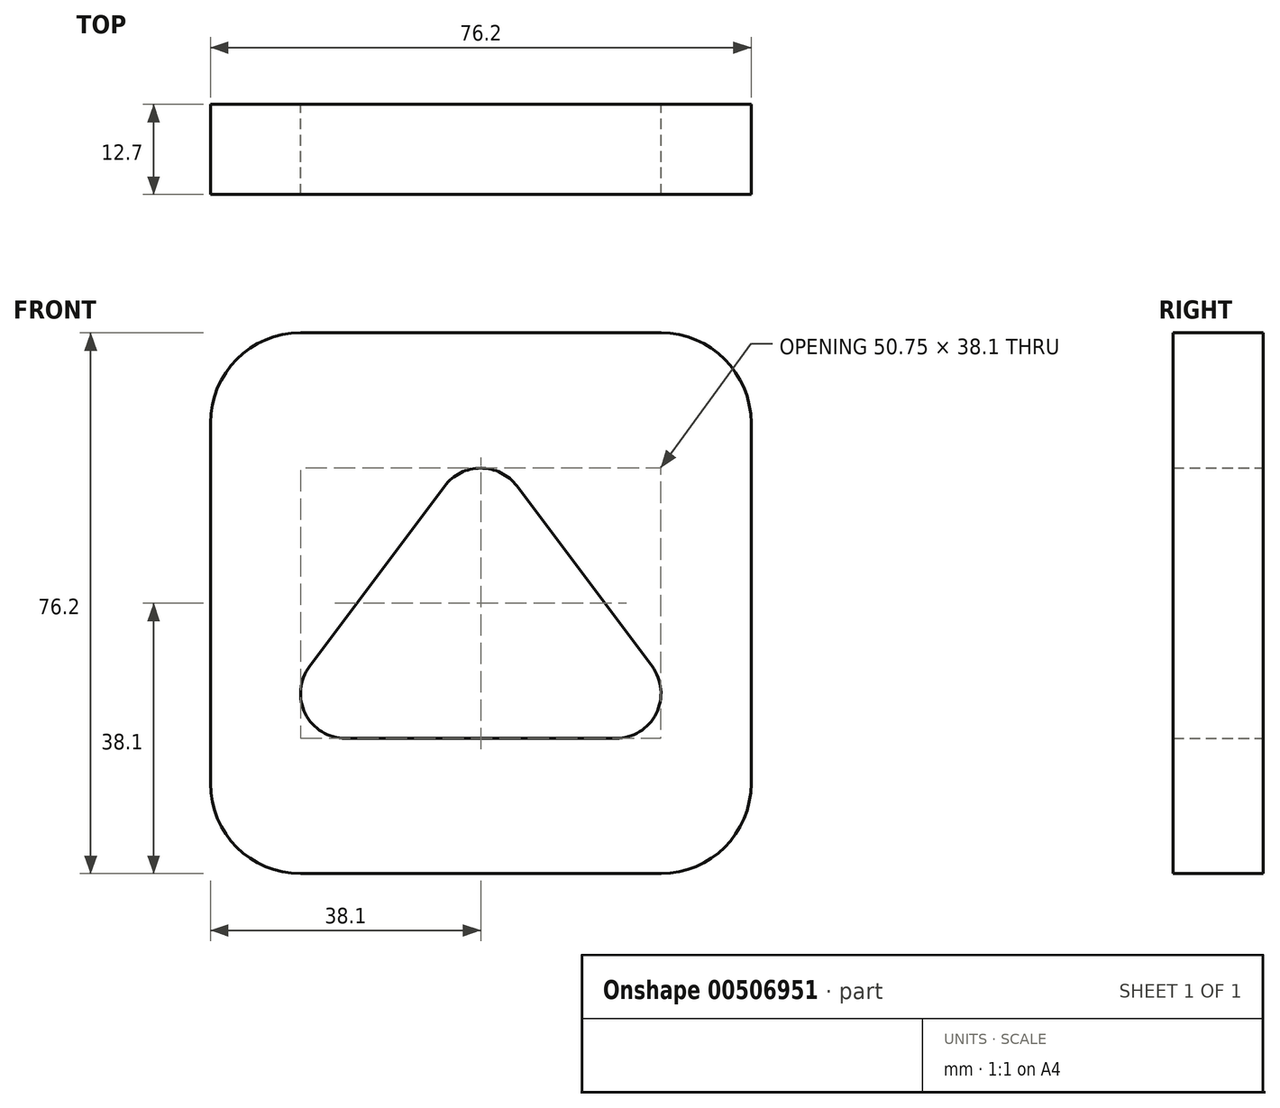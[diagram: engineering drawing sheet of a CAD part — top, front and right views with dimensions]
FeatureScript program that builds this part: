
annotation { "Feature Type Name" : "Feature", "Feature Type Description" : "" }
export const myFeature = defineFeature(function(context is Context, id is Id, definition is map)
    precondition{}
    {
        {
            var Q0;
            Q0=qCreatedBy(makeId("Front.planeOp"),FACE);
            var sketch = newSketch(context, id + "F0", { "sketchPlane" : qUnion([Q0])});
            skLineSegment(sketch, "E0", {"start": v(12.7, 0) * mm, "end": v(65.14, 0) * mm});
            skLineSegment(sketch, "E1", {"start": v(76.2, 11.06) * mm, "end": v(76.2, 63.5) * mm});
            skLineSegment(sketch, "E2", {"start": v(63.5, 76.2) * mm, "end": v(12.7, 76.2) * mm});
            skLineSegment(sketch, "E3", {"start": v(0, 63.5) * mm, "end": v(0, 15.9) * mm});
            skArc(sketch, "E4", {"start": v(13.97, 29.21) * mm, "mid": v(13.37, 22.56) * mm, "end": v(19.05, 19.05) * mm});
            skArc(sketch, "E5", {"start": v(57.15, 19.05) * mm, "mid": v(62.83, 22.56) * mm, "end": v(62.23, 29.21) * mm});
            skArc(sketch, "E6", {"start": v(43.18, 54.6) * mm, "mid": v(38.1, 57.15) * mm, "end": v(33.02, 54.61) * mm});
            skLineSegment(sketch, "E7", {"start": v(33.02, 54.61) * mm, "end": v(13.97, 29.2) * mm});
            skLineSegment(sketch, "E8", {"start": v(43.18, 54.6) * mm, "end": v(62.23, 29.21) * mm});
            skLineSegment(sketch, "E9", {"start": v(19.05, 19.05) * mm, "end": v(57.15, 19.05) * mm});
            skArc(sketch, "E10", {"start": v(12.7, 76.2) * mm, "mid": v(3.72, 72.48) * mm, "end": v(0, 63.5) * mm});
            skPoint(sketch, "E11.orphan", {"position": v(0, 76.2) * mm});
            skArc(sketch, "E12", {"start": v(76.2, 63.5) * mm, "mid": v(72.48, 72.48) * mm, "end": v(63.5, 76.2) * mm});
            skArc(sketch, "E13.trimOffspring", {"start": v(62.35, 21.76) * mm, "mid": v(59.76, 20.72) * mm, "end": v(57.51, 19.06) * mm});
            skLineSegment(sketch, "E14", {"start": v(0, 15.9) * mm, "end": v(0, 12.7) * mm});
            skArc(sketch, "E15", {"start": v(0, 12.7) * mm, "mid": v(3.72, 3.72) * mm, "end": v(12.7, 0) * mm});
            skArc(sketch, "E16", {"start": v(63.5, 0) * mm, "mid": v(72.48, 3.72) * mm, "end": v(76.2, 12.7) * mm});
            skPoint(sketch, "E17.end.orphan", {"position": v(76.2, 0) * mm});
            skSolve(sketch);
        }
        {
            var Q0;
            Q0=makeQuery(id+"F0.imprint","IMPRINT",FACE,{"disambiguationData":[TD([[makeQuery(id+"F0.imprint","IMPRINT",EDGE,{"derivedFrom":sQuery(id+"F0.wireOp",EDGE,"E2")}),1.0]])]});
            extrude(context, id + "F1", {"entities" : qUnion([Q0]), "depth" : 12.7 * mm});
        }
    });
